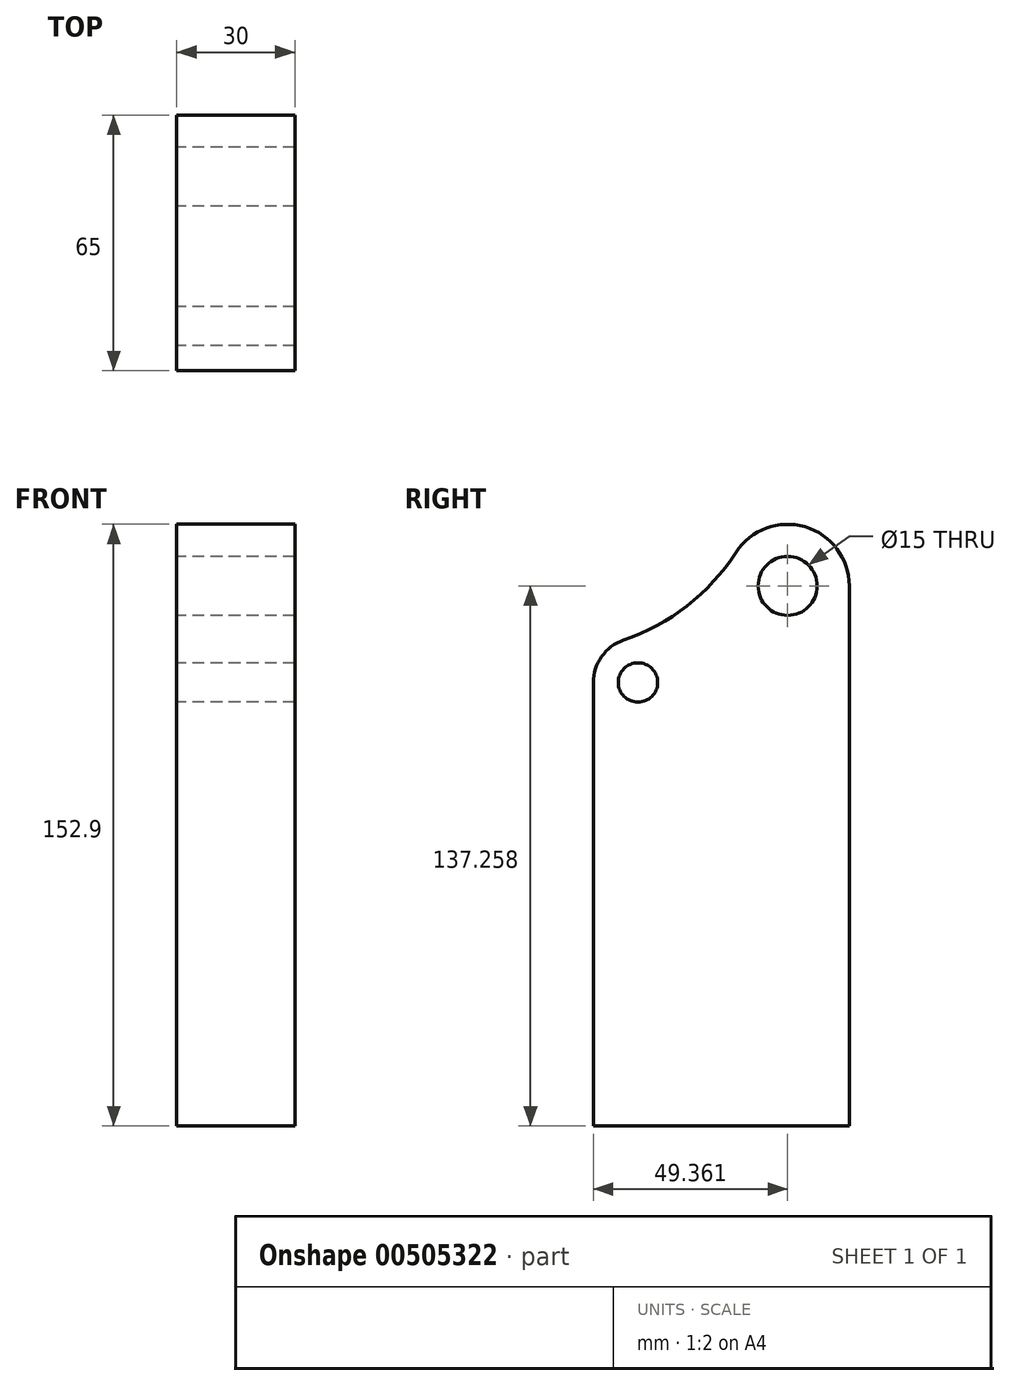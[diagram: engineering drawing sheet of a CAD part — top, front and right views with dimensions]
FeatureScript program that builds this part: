
annotation { "Feature Type Name" : "Feature", "Feature Type Description" : "" }
export const myFeature = defineFeature(function(context is Context, id is Id, definition is map)
    precondition{}
    {
        {
            var Q0;
            Q0=qCreatedBy(makeId("Right.planeOp"),FACE);
            var sketch = newSketch(context, id + "F0", { "sketchPlane" : qUnion([Q0])});
            skLineSegment(sketch, "E0.top", {"start": v(0, 0) * mm, "end": v(65, 0) * mm});
            skLineSegment(sketch, "E0.left", {"start": v(0, 100) * mm, "end": v(0, 0) * mm});
            skLineSegment(sketch, "E0.right", {"start": v(65, 100) * mm, "end": v(65, 0) * mm});
            skCircle(sketch, "E1", {"center": v(49.36, 137.26) * mm, "radius": 7.5 * mm});
            skCircle(sketch, "E2", {"center": v(11.34, 112.7) * mm, "radius": 5 * mm});
            skLineSegment(sketch, "E3", {"start": v(0, 100) * mm, "end": v(0, 112.7) * mm});
            skLineSegment(sketch, "E4", {"start": v(65, 100) * mm, "end": v(65, 137.26) * mm});
            skArc(sketch, "E5", {"start": v(7.68, 123.44) * mm, "mid": v(23.83, 132.18) * mm, "end": v(36.22, 145.74) * mm});
            skArc(sketch, "E6", {"start": v(65, 137.26) * mm, "mid": v(53.78, 152.26) * mm, "end": v(36.22, 145.74) * mm});
            skArc(sketch, "E7", {"start": v(0, 112.7) * mm, "mid": v(2.12, 119.3) * mm, "end": v(7.68, 123.44) * mm});
            skLineSegment(sketch, "E8", {"start": v(-135.57, 0) * mm, "end": v(-151.79, 115.39) * mm});
            skCircle(sketch, "E9", {"center": v(-205.01, 130.77) * mm, "radius": 7.5 * mm});
            skCircle(sketch, "E10", {"center": v(-163.74, 113.7) * mm, "radius": 5 * mm});
            skArc(sketch, "E11", {"start": v(-151.79, 115.39) * mm, "mid": v(-155.6, 122.63) * mm, "end": v(-163.16, 125.77) * mm});
            skArc(sketch, "E12", {"start": v(-219.3, 128.76) * mm, "mid": v(-211.14, 143.83) * mm, "end": v(-194.33, 140.47) * mm});
            skArc(sketch, "E13", {"start": v(-194.33, 140.47) * mm, "mid": v(-180.2, 130.02) * mm, "end": v(-163.16, 125.77) * mm});
            skLineSegment(sketch, "E14", {"start": v(-135.57, 0) * mm, "end": v(-201.2, 0) * mm});
            skLineSegment(sketch, "E15", {"start": v(-201.2, 0) * mm, "end": v(-219.3, 128.76) * mm});
            skSolve(sketch);
        }
        {
            var Q0;
            Q0=makeQuery(id+"F0.imprint","IMPRINT",FACE,{"disambiguationData":[TD([[makeQuery(id+"F0.imprint","IMPRINT",EDGE,{"derivedFrom":sQuery(id+"F0.wireOp",EDGE,"E0.top")}),1.0]])]});
            extrude(context, id + "F1", {"entities" : qUnion([Q0]), "depth" : 30 * mm, "offsetDistance" : 25 * mm, "symmetric" : true});
        }
    });
